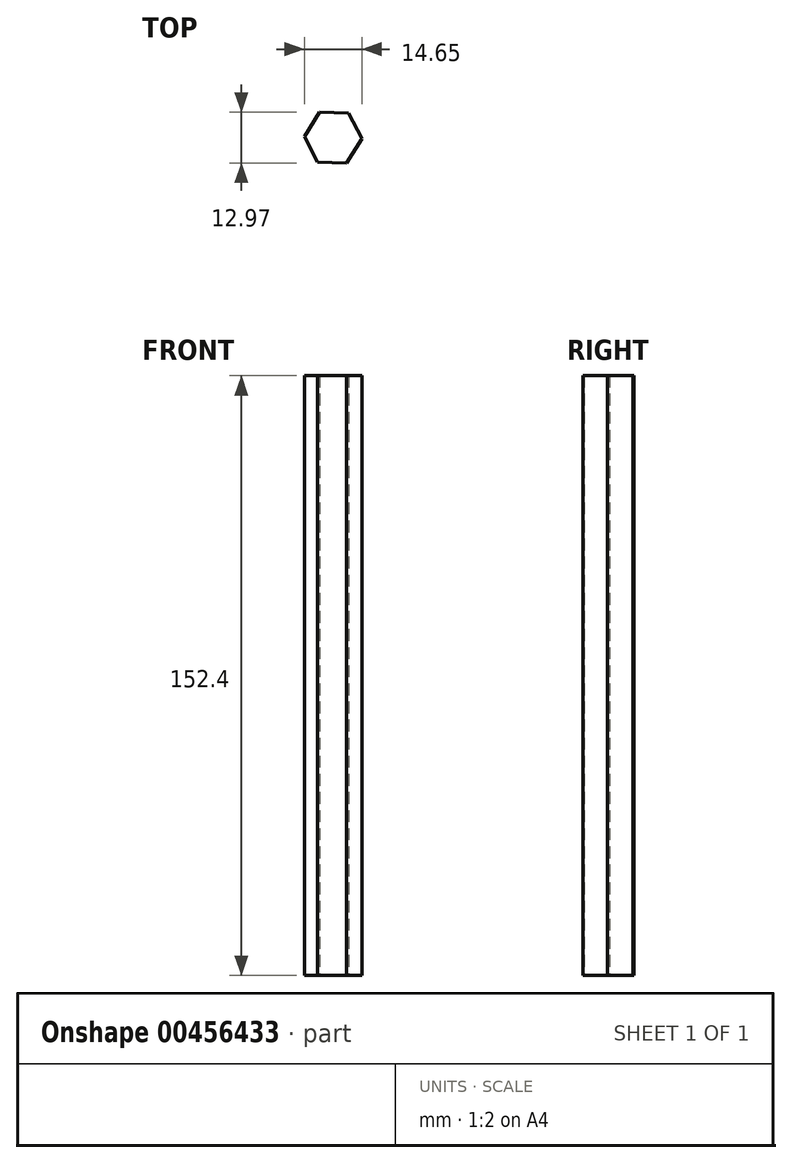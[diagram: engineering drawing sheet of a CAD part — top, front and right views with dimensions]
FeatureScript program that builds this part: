
annotation { "Feature Type Name" : "Feature", "Feature Type Description" : "" }
export const myFeature = defineFeature(function(context is Context, id is Id, definition is map)
    precondition{}
    {
        {
            var Q0;
            Q0=qCreatedBy(makeId("Top.planeOp"),FACE);
            var sketch = newSketch(context, id + "F0", { "sketchPlane" : qUnion([Q0])});
            skCircle(sketch, "E0.cCircle", {"center": v(-53.72, -42.1) * mm, "radius": 6.35 * mm, "construction": true});
            skLineSegment(sketch, "E0.0", {"start": v(-46.39, -42.38) * mm, "end": v(-50.3, -48.59) * mm});
            skLineSegment(sketch, "E0.1", {"start": v(-50.3, -48.59) * mm, "end": v(-57.62, -48.3) * mm});
            skLineSegment(sketch, "E0.2", {"start": v(-57.62, -48.3) * mm, "end": v(-61.04, -41.82) * mm});
            skLineSegment(sketch, "E0.3", {"start": v(-61.04, -41.82) * mm, "end": v(-57.14, -35.62) * mm});
            skLineSegment(sketch, "E0.4", {"start": v(-57.14, -35.62) * mm, "end": v(-49.81, -35.9) * mm});
            skLineSegment(sketch, "E0.5", {"start": v(-49.81, -35.9) * mm, "end": v(-46.39, -42.38) * mm});
            skPoint(sketch, "E0.0.midPoint", {"position": v(-48.34, -45.48) * mm});
            skSolve(sketch);
        }
        {
            var Q0;
            Q0=makeQuery(id+"F0.imprint","IMPRINT",FACE,{"disambiguationData":[TD([[makeQuery(id+"F0.imprint","IMPRINT",EDGE,{"derivedFrom":sQuery(id+"F0.wireOp",EDGE,"E0.0")}),-1.0]])]});
            extrude(context, id + "F1", {"entities" : qUnion([Q0]), "depth" : 152.4 * mm});
        }
    });
